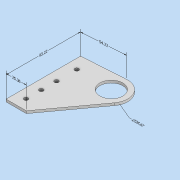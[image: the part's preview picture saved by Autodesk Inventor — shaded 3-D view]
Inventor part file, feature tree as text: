
AUTODESK INVENTOR PART (.ipt)
format: ipt  version: 2022 (Build 260153000, 153)  size: 126,976 bytes
history: native  units: in
note: dims shown in document units (in); Inventor stores cm internally (conversion verified against a paired STEP export)
features: other x5, extrude x1, sketch x1
ambient origin geometry x8: Origin, YZ Plane, XZ Plane, XY Plane, X Axis, Y Axis, Z Axis, Center Point
bodies: Body1 (feature_tree)
feature tree (7):
  other  "Annotations"
  extrude  "Extrusion2"  Depth=0.9984in
  sketch  "Sketch1"  dims[d1=0.9984in d2=3.6701in d3=0.4803in d4=0.4043in d5=0.0984in d10=0.5535in d11=0.0984in d12=0.5535in d13=0.0984in d14=0.8031in d15=0.0984in d16=1.0425in d17=0.562in d25=1.1268in d26=0.2457in d27=0.1209in d28=0.0in d29=2.3953in d30=1.1268in d32=0.0in d33=0.3937in d34=3.6701in d35=0.0in d36=0.3937in d37=2.1346in d38=0.0in d39=0.3937in d40=0.9984in]
  other  "Diameter Dimension 1"
  other  "Linear Dimension 1"
  other  "Linear Dimension 2"
  other  "Linear Dimension 3"
